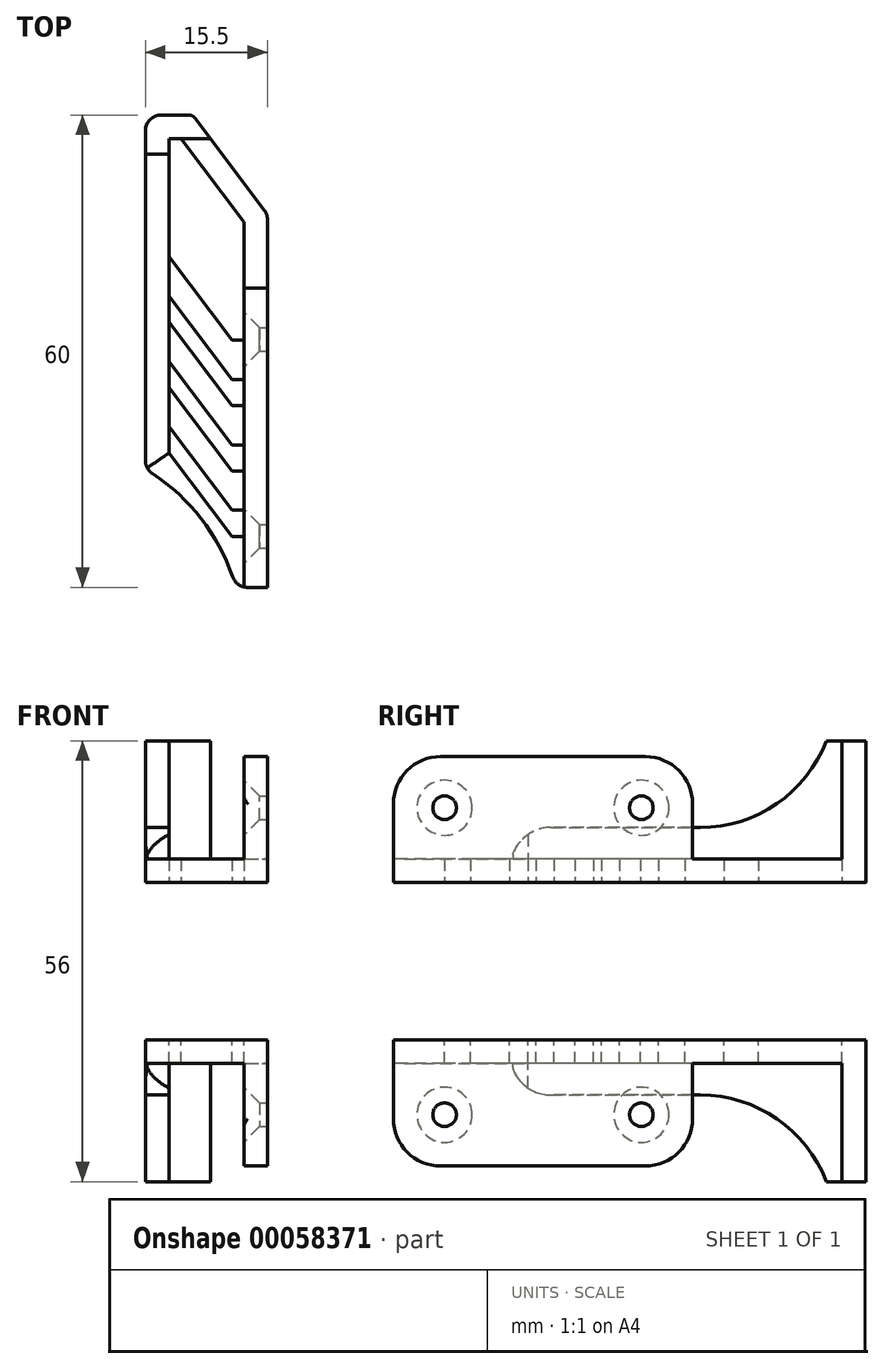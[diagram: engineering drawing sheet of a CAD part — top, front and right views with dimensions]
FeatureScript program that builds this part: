
annotation { "Feature Type Name" : "Feature", "Feature Type Description" : "" }
export const myFeature = defineFeature(function(context is Context, id is Id, definition is map)
    precondition{}
    {
        {
            var Q0;
            Q0=qCreatedBy(makeId("Top.planeOp"),FACE);
            var sketch = newSketch(context, id + "F0", { "sketchPlane" : qUnion([Q0])});
            skLineSegment(sketch, "E0", {"start": v(0, 30) * mm, "end": v(6, 30) * mm});
            skLineSegment(sketch, "E1", {"start": v(6, 30) * mm, "end": v(15.5, 17.4) * mm});
            skLineSegment(sketch, "E2", {"start": v(15.5, 17.4) * mm, "end": v(15.5, -30) * mm});
            skLineSegment(sketch, "E3", {"start": v(15.5, -30) * mm, "end": v(11.5, -30) * mm});
            skLineSegment(sketch, "E4", {"start": v(0, 30) * mm, "end": v(0, -15) * mm});
            skArc(sketch, "E5", {"start": v(11.5, -30) * mm, "mid": v(7.2, -21.4) * mm, "end": v(0, -15) * mm});
            skLineSegment(sketch, "E6", {"start": v(12.5, 16.39) * mm, "end": v(4.5, 27) * mm});
            skLineSegment(sketch, "E7", {"start": v(4.5, 27) * mm, "end": v(3, 27) * mm});
            skLineSegment(sketch, "E8", {"start": v(3, 27) * mm, "end": v(3, 12) * mm});
            skLineSegment(sketch, "E9", {"start": v(3, 12) * mm, "end": v(11, 1.39) * mm});
            skLineSegment(sketch, "E10", {"start": v(11, 1.39) * mm, "end": v(12.5, 1.39) * mm});
            skLineSegment(sketch, "E11", {"start": v(12.5, 1.39) * mm, "end": v(12.5, 16.39) * mm});
            skLineSegment(sketch, "E12", {"start": v(3, 7.02) * mm, "end": v(11, -3.6) * mm});
            skLineSegment(sketch, "E13", {"start": v(11, -3.6) * mm, "end": v(12.5, -3.6) * mm});
            skLineSegment(sketch, "E14", {"start": v(12.5, -3.6) * mm, "end": v(12.5, -6.92) * mm});
            skLineSegment(sketch, "E15", {"start": v(3, 7.02) * mm, "end": v(3, 3.7) * mm});
            skLineSegment(sketch, "E16", {"start": v(3, 3.7) * mm, "end": v(11, -6.92) * mm});
            skLineSegment(sketch, "E17", {"start": v(11, -6.92) * mm, "end": v(12.5, -6.92) * mm});
            skLineSegment(sketch, "E18", {"start": v(3, -4.62) * mm, "end": v(11, -15.23) * mm});
            skLineSegment(sketch, "E19", {"start": v(11, -11.9) * mm, "end": v(12.5, -11.9) * mm});
            skLineSegment(sketch, "E20", {"start": v(11, -15.23) * mm, "end": v(12.5, -15.23) * mm});
            skLineSegment(sketch, "E21", {"start": v(3, -1.3) * mm, "end": v(11, -11.9) * mm});
            skLineSegment(sketch, "E22", {"start": v(12.5, -11.9) * mm, "end": v(12.5, -15.23) * mm});
            skLineSegment(sketch, "E23", {"start": v(3, -1.3) * mm, "end": v(3, -4.62) * mm});
            skLineSegment(sketch, "E24", {"start": v(11, -20.21) * mm, "end": v(12.5, -20.21) * mm});
            skLineSegment(sketch, "E25", {"start": v(3, -12.92) * mm, "end": v(11, -23.54) * mm});
            skLineSegment(sketch, "E26", {"start": v(12.5, -20.21) * mm, "end": v(12.5, -23.54) * mm});
            skLineSegment(sketch, "E27", {"start": v(11, -23.54) * mm, "end": v(12.5, -23.54) * mm});
            skLineSegment(sketch, "E28", {"start": v(3, -9.6) * mm, "end": v(3, -12.92) * mm});
            skLineSegment(sketch, "E29", {"start": v(3, -9.6) * mm, "end": v(11, -20.21) * mm});
            skSolve(sketch);
        }
        {
            var Q0;
            Q0=makeQuery(id+"F0.imprint","IMPRINT",FACE,{"disambiguationData":[TD([[makeQuery(id+"F0.imprint","IMPRINT",EDGE,{"derivedFrom":sQuery(id+"F0.wireOp",EDGE,"E0")}),-1.0]])]});
            extrude(context, id + "F1", {"entities" : qUnion([Q0]), "depth" : 3 * mm});
        }
        {
            var Q0;
            Q0=makeQuery(id+"F1.opExtrude","SWEPT_FACE",FACE,{"disambiguationData":[OSD([sQuery(id+"F0.wireOp",EDGE,"E2")])]});
            var sketch = newSketch(context, id + "F2", { "sketchPlane" : qUnion([Q0])});
            skLineSegment(sketch, "E30.0", {"start": v(17.4, 3) * mm, "end": v(-30, 3) * mm});
            skLineSegment(sketch, "E31", {"start": v(-30, 3) * mm, "end": v(-30, 10) * mm});
            skLineSegment(sketch, "E32", {"start": v(-24, 16) * mm, "end": v(2, 16) * mm});
            skLineSegment(sketch, "E33", {"start": v(8, 10) * mm, "end": v(8, 3) * mm});
            skCircle(sketch, "E34", {"center": v(-23.5, 9.5) * mm, "radius": 1.5 * mm});
            skCircle(sketch, "E35", {"center": v(1.5, 9.5) * mm, "radius": 1.5 * mm});
            skPoint(sketch, "E36.visualSharp", {"position": v(-30, 16) * mm});
            skArc(sketch, "E36.filletArc", {"start": v(-24, 16) * mm, "mid": v(-28.24, 14.24) * mm, "end": v(-30, 10) * mm});
            skPoint(sketch, "E37.visualSharp", {"position": v(8, 16) * mm});
            skArc(sketch, "E37.filletArc", {"start": v(8, 10) * mm, "mid": v(6.24, 14.24) * mm, "end": v(2, 16) * mm});
            skSolve(sketch);
        }
        {
            var Q0;
            {var subQ1=sQuery(id+"F2.wireOp",EDGE,"E31");Q0=makeQuery(id+"F2.imprint","IMPRINT",FACE,{"disambiguationData":[TD([[makeQuery(id+"F2.imprint","IMPRINT",EDGE,{"derivedFrom":subQ1}),-1.0]])]});}
            extrude(context, id + "F3", {"entities" : qUnion([Q0]), "operationType" : NewBodyOperationType.ADD, "oppositeDirection" : true, "depth" : 3 * mm});
        }
        {
            var Q0;
            Q0=makeQuery(id+"F3.opExtrude","CAP_EDGE",EDGE,{"disambiguationData":[OSD([sQuery(id+"F2.wireOp",EDGE,"E34")])],"isStart":false});
            var Q1;
            Q1=makeQuery(id+"F3.opExtrude","CAP_EDGE",EDGE,{"disambiguationData":[OSD([sQuery(id+"F2.wireOp",EDGE,"E35")])],"isStart":false});
            chamfer(context, id + "F4", {"entities" : qUnion([Q0, Q1]), "width" : 2 * mm, "tangentPropagation" : true});
        }
        {
            var Q0;
            Q0=makeQuery(id+"F1.opExtrude","CAP_FACE",FACE,{"disambiguationData":[OSD([sQuery(id+"F0.wireOp",EDGE,"E0"),sQuery(id+"F0.wireOp",EDGE,"E1"),sQuery(id+"F0.wireOp",EDGE,"E2"),sQuery(id+"F0.wireOp",EDGE,"E3"),sQuery(id+"F0.wireOp",EDGE,"E4"),sQuery(id+"F0.wireOp",EDGE,"E5"),sQuery(id+"F0.wireOp",EDGE,"E6"),sQuery(id+"F0.wireOp",EDGE,"E7"),sQuery(id+"F0.wireOp",EDGE,"E8"),sQuery(id+"F0.wireOp",EDGE,"E9"),sQuery(id+"F0.wireOp",EDGE,"E10"),sQuery(id+"F0.wireOp",EDGE,"E11"),sQuery(id+"F0.wireOp",EDGE,"E12"),sQuery(id+"F0.wireOp",EDGE,"E13"),sQuery(id+"F0.wireOp",EDGE,"E14"),sQuery(id+"F0.wireOp",EDGE,"E15"),sQuery(id+"F0.wireOp",EDGE,"E16"),sQuery(id+"F0.wireOp",EDGE,"E17"),sQuery(id+"F0.wireOp",EDGE,"E18"),sQuery(id+"F0.wireOp",EDGE,"E19"),sQuery(id+"F0.wireOp",EDGE,"E20"),sQuery(id+"F0.wireOp",EDGE,"E21"),sQuery(id+"F0.wireOp",EDGE,"E22"),sQuery(id+"F0.wireOp",EDGE,"E23"),sQuery(id+"F0.wireOp",EDGE,"E24"),sQuery(id+"F0.wireOp",EDGE,"E25"),sQuery(id+"F0.wireOp",EDGE,"E26"),sQuery(id+"F0.wireOp",EDGE,"E27"),sQuery(id+"F0.wireOp",EDGE,"E28"),sQuery(id+"F0.wireOp",EDGE,"E29")])],"isStart":false});
            var sketch = newSketch(context, id + "F5", { "sketchPlane" : qUnion([Q0])});
            skLineSegment(sketch, "E38.0", {"start": v(0, 30) * mm, "end": v(0, -15) * mm});
            skLineSegment(sketch, "E38.1", {"start": v(0, 30) * mm, "end": v(6, 30) * mm});
            skLineSegment(sketch, "E39", {"start": v(0, -15) * mm, "end": v(3, -12.92) * mm});
            skLineSegment(sketch, "E40", {"start": v(3, -12.92) * mm, "end": v(3, 27) * mm});
            skLineSegment(sketch, "E41", {"start": v(3, 27) * mm, "end": v(4.5, 27) * mm});
            skLineSegment(sketch, "E42", {"start": v(4.5, 27) * mm, "end": v(8.26, 27) * mm});
            skLineSegment(sketch, "E43", {"start": v(8.26, 27) * mm, "end": v(6, 30) * mm});
            skSolve(sketch);
        }
        {
            var Q0;
            Q0 = qSketchRegion(id + "F5", true);
            extrude(context, id + "F6", {"entities" : qUnion([Q0]), "operationType" : NewBodyOperationType.ADD, "depth" : 15 * mm});
        }
        {
            var Q0;
            Q0=makeQuery(id+"F6.boolean.opBoolean","MERGE",FACE,{"derivedFrom":[makeQuery(id+"F1.opExtrude","SWEPT_FACE",FACE,{"disambiguationData":[OSD([sQuery(id+"F0.wireOp",EDGE,"E4")])]}),makeQuery(id+"F6.opExtrude","SWEPT_FACE",FACE,{"disambiguationData":[OSD([sQuery(id+"F5.wireOp",EDGE,"E38.0")])]})]});
            var sketch = newSketch(context, id + "F7", { "sketchPlane" : qUnion([Q0])});
            skLineSegment(sketch, "E44", {"start": v(10, 7) * mm, "end": v(-9, 7) * mm});
            skArc(sketch, "E45", {"start": v(-25, 18) * mm, "mid": v(-18.7, 10.02) * mm, "end": v(-9, 7) * mm});
            skArc(sketch, "E46", {"start": v(15, 3) * mm, "mid": v(13.2, 5.88) * mm, "end": v(10, 7) * mm});
            skLineSegment(sketch, "E47.0", {"start": v(-30, 18) * mm, "end": v(15, 18) * mm});
            skLineSegment(sketch, "E47.1", {"start": v(15, 18) * mm, "end": v(15, 3) * mm});
            skSolve(sketch);
        }
        {
            var Q0;
            Q0=makeQuery(id+"F7.imprint","IMPRINT",FACE,{"disambiguationData":[TD([[makeQuery(id+"F7.imprint","IMPRINT",EDGE,{"derivedFrom":sQuery(id+"F7.wireOp",EDGE,"E44")}),-1.0]])]});
            extrude(context, id + "F8", {"entities" : qUnion([Q0]), "operationType" : NewBodyOperationType.REMOVE, "oppositeDirection" : true, "depth" : 5 * mm});
        }
        {
            var Q0;
            Q0=makeQuery(id+"F6.boolean.opBoolean","MERGE",EDGE,{"derivedFrom":[makeQuery(id+"F1.opExtrude","SWEPT_EDGE",EDGE,{"disambiguationData":[OSD([sQuery(id+"F0.wireOp",EDGE,"E0"),sQuery(id+"F0.wireOp",EDGE,"E4")])]}),makeQuery(id+"F6.opExtrude","SWEPT_EDGE",EDGE,{"disambiguationData":[OSD([sQuery(id+"F5.wireOp",EDGE,"E38.0"),sQuery(id+"F5.wireOp",EDGE,"E38.1")])]})]});
            var Q1;
            Q1=makeQuery(id+"F1.opExtrude","SWEPT_EDGE",EDGE,{"disambiguationData":[OSD([sQuery(id+"F0.wireOp",EDGE,"E4"),sQuery(id+"F0.wireOp",EDGE,"E5")])]});
            var Q2;
            Q2=makeQuery(id+"F1.opExtrude","SWEPT_EDGE",EDGE,{"disambiguationData":[OSD([sQuery(id+"F0.wireOp",EDGE,"E3"),sQuery(id+"F0.wireOp",EDGE,"E5")])]});
            var Q3;
            Q3=makeQuery(id+"F1.opExtrude","SWEPT_EDGE",EDGE,{"disambiguationData":[OSD([sQuery(id+"F0.wireOp",EDGE,"E1"),sQuery(id+"F0.wireOp",EDGE,"E2")])]});
            fillet(context, id + "F9", {"entities" : qUnion([Q0, Q1, Q2, Q3]), "radius" : 2 * mm, "tangentPropagation" : true, "allowEdgeOverflow" : false});
        }
        {
            var Q0;
            Q0=makeQuery(id+"F6.boolean.opBoolean","MERGE",EDGE,{"derivedFrom":[makeQuery(id+"F1.opExtrude","SWEPT_EDGE",EDGE,{"disambiguationData":[OSD([sQuery(id+"F0.wireOp",EDGE,"E0"),sQuery(id+"F0.wireOp",EDGE,"E1")])]}),makeQuery(id+"F6.opExtrude","SWEPT_EDGE",EDGE,{"disambiguationData":[OSD([sQuery(id+"F5.wireOp",EDGE,"E38.1"),sQuery(id+"F5.wireOp",EDGE,"E43")])]})]});
            fillet(context, id + "F10", {"entities" : qUnion([Q0]), "radius" : 1 * mm, "tangentPropagation" : true, "allowEdgeOverflow" : false});
        }
        {
            var Q0;
            Q0=makeQuery(id+"F1.opExtrude","SWEPT_BODY",BODY,{"disambiguationData":[OSD([sQuery(id+"F0.wireOp",EDGE,"E0"),sQuery(id+"F0.wireOp",EDGE,"E1"),sQuery(id+"F0.wireOp",EDGE,"E2"),sQuery(id+"F0.wireOp",EDGE,"E3"),sQuery(id+"F0.wireOp",EDGE,"E4"),sQuery(id+"F0.wireOp",EDGE,"E5"),sQuery(id+"F0.wireOp",EDGE,"E6"),sQuery(id+"F0.wireOp",EDGE,"E7"),sQuery(id+"F0.wireOp",EDGE,"E8"),sQuery(id+"F0.wireOp",EDGE,"E9"),sQuery(id+"F0.wireOp",EDGE,"E10"),sQuery(id+"F0.wireOp",EDGE,"E11"),sQuery(id+"F0.wireOp",EDGE,"E12"),sQuery(id+"F0.wireOp",EDGE,"E13"),sQuery(id+"F0.wireOp",EDGE,"E14"),sQuery(id+"F0.wireOp",EDGE,"E15"),sQuery(id+"F0.wireOp",EDGE,"E16"),sQuery(id+"F0.wireOp",EDGE,"E17"),sQuery(id+"F0.wireOp",EDGE,"E18"),sQuery(id+"F0.wireOp",EDGE,"E19"),sQuery(id+"F0.wireOp",EDGE,"E20"),sQuery(id+"F0.wireOp",EDGE,"E21"),sQuery(id+"F0.wireOp",EDGE,"E22"),sQuery(id+"F0.wireOp",EDGE,"E23"),sQuery(id+"F0.wireOp",EDGE,"E24"),sQuery(id+"F0.wireOp",EDGE,"E25"),sQuery(id+"F0.wireOp",EDGE,"E26"),sQuery(id+"F0.wireOp",EDGE,"E27"),sQuery(id+"F0.wireOp",EDGE,"E28"),sQuery(id+"F0.wireOp",EDGE,"E29")])]});
            var Q1;
            Q1=qCreatedBy(makeId("Top.planeOp"),FACE);
            mirror(context, id + "F11", {"entities" : qUnion([Q0]), "mirrorPlane" : qUnion([Q1])});
        }
        {
            var Q0;
            Q0=makeQuery(id+"F1.opExtrude","SWEPT_BODY",BODY,{"disambiguationData":[OSD([sQuery(id+"F0.wireOp",EDGE,"E0"),sQuery(id+"F0.wireOp",EDGE,"E1"),sQuery(id+"F0.wireOp",EDGE,"E2"),sQuery(id+"F0.wireOp",EDGE,"E3"),sQuery(id+"F0.wireOp",EDGE,"E4"),sQuery(id+"F0.wireOp",EDGE,"E5"),sQuery(id+"F0.wireOp",EDGE,"E6"),sQuery(id+"F0.wireOp",EDGE,"E7"),sQuery(id+"F0.wireOp",EDGE,"E8"),sQuery(id+"F0.wireOp",EDGE,"E9"),sQuery(id+"F0.wireOp",EDGE,"E10"),sQuery(id+"F0.wireOp",EDGE,"E11"),sQuery(id+"F0.wireOp",EDGE,"E12"),sQuery(id+"F0.wireOp",EDGE,"E13"),sQuery(id+"F0.wireOp",EDGE,"E14"),sQuery(id+"F0.wireOp",EDGE,"E15"),sQuery(id+"F0.wireOp",EDGE,"E16"),sQuery(id+"F0.wireOp",EDGE,"E17"),sQuery(id+"F0.wireOp",EDGE,"E18"),sQuery(id+"F0.wireOp",EDGE,"E19"),sQuery(id+"F0.wireOp",EDGE,"E20"),sQuery(id+"F0.wireOp",EDGE,"E21"),sQuery(id+"F0.wireOp",EDGE,"E22"),sQuery(id+"F0.wireOp",EDGE,"E23"),sQuery(id+"F0.wireOp",EDGE,"E24"),sQuery(id+"F0.wireOp",EDGE,"E25"),sQuery(id+"F0.wireOp",EDGE,"E26"),sQuery(id+"F0.wireOp",EDGE,"E27"),sQuery(id+"F0.wireOp",EDGE,"E28"),sQuery(id+"F0.wireOp",EDGE,"E29")])]});
            transform(context, id + "F12", {"entities" : qUnion([Q0]), "transformType" : TransformType.TRANSLATION_3D, "dx" : 0 * mm, "dy" : 0 * mm, "dz" : 10 * mm, "makeCopy" : false});
        }
        {
            var Q0;
            Q0=makeQuery(id+"F11.opPattern","COPY",BODY,{"derivedFrom":makeQuery(id+"F1.opExtrude","SWEPT_BODY",BODY,{"disambiguationData":[OSD([sQuery(id+"F0.wireOp",EDGE,"E0"),sQuery(id+"F0.wireOp",EDGE,"E1"),sQuery(id+"F0.wireOp",EDGE,"E2"),sQuery(id+"F0.wireOp",EDGE,"E3"),sQuery(id+"F0.wireOp",EDGE,"E4"),sQuery(id+"F0.wireOp",EDGE,"E5"),sQuery(id+"F0.wireOp",EDGE,"E6"),sQuery(id+"F0.wireOp",EDGE,"E7"),sQuery(id+"F0.wireOp",EDGE,"E8"),sQuery(id+"F0.wireOp",EDGE,"E9"),sQuery(id+"F0.wireOp",EDGE,"E10"),sQuery(id+"F0.wireOp",EDGE,"E11"),sQuery(id+"F0.wireOp",EDGE,"E12"),sQuery(id+"F0.wireOp",EDGE,"E13"),sQuery(id+"F0.wireOp",EDGE,"E14"),sQuery(id+"F0.wireOp",EDGE,"E15"),sQuery(id+"F0.wireOp",EDGE,"E16"),sQuery(id+"F0.wireOp",EDGE,"E17"),sQuery(id+"F0.wireOp",EDGE,"E18"),sQuery(id+"F0.wireOp",EDGE,"E19"),sQuery(id+"F0.wireOp",EDGE,"E20"),sQuery(id+"F0.wireOp",EDGE,"E21"),sQuery(id+"F0.wireOp",EDGE,"E22"),sQuery(id+"F0.wireOp",EDGE,"E23"),sQuery(id+"F0.wireOp",EDGE,"E24"),sQuery(id+"F0.wireOp",EDGE,"E25"),sQuery(id+"F0.wireOp",EDGE,"E26"),sQuery(id+"F0.wireOp",EDGE,"E27"),sQuery(id+"F0.wireOp",EDGE,"E28"),sQuery(id+"F0.wireOp",EDGE,"E29")])]}),"instanceName":"1"});
            transform(context, id + "F13", {"entities" : qUnion([Q0]), "transformType" : TransformType.TRANSLATION_3D, "dx" : 0 * mm, "dy" : 0 * mm, "dz" : -10 * mm, "makeCopy" : false});
        }
    });
